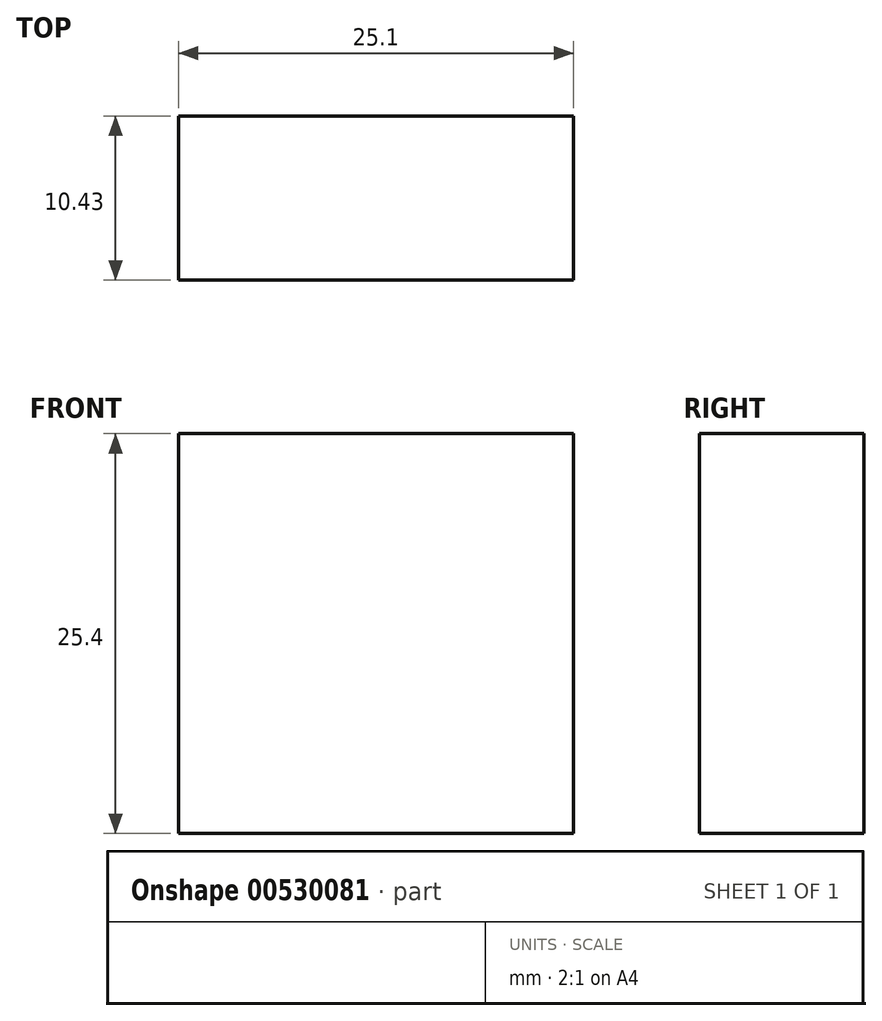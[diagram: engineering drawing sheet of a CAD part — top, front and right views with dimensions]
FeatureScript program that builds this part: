
annotation { "Feature Type Name" : "Feature", "Feature Type Description" : "" }
export const myFeature = defineFeature(function(context is Context, id is Id, definition is map)
    precondition{}
    {
        {
            var Q0;
            Q0=qCreatedBy(makeId("Top.planeOp"),FACE);
            var sketch = newSketch(context, id + "F0", { "sketchPlane" : qUnion([Q0])});
            skLineSegment(sketch, "E0", {"start": v(45.07, -18.4) * mm, "end": v(-42.5, -6.13) * mm});
            skLineSegment(sketch, "E1", {"start": v(-38.27, -6.73) * mm, "end": v(-38.27, 20.97) * mm});
            skLineSegment(sketch, "E2", {"start": v(-38.27, 20.97) * mm, "end": v(-23.96, 29.8) * mm});
            skLineSegment(sketch, "E3", {"start": v(-38.27, 20.97) * mm, "end": v(-57.62, 29.8) * mm});
            skLineSegment(sketch, "E4", {"start": v(16.5, -14.4) * mm, "end": v(19.96, 10.25) * mm});
            skLineSegment(sketch, "E5.bottom", {"start": v(7.13, 20.68) * mm, "end": v(32.23, 20.68) * mm});
            skLineSegment(sketch, "E5.top", {"start": v(7.13, 10.25) * mm, "end": v(32.23, 10.25) * mm});
            skLineSegment(sketch, "E5.left", {"start": v(7.13, 20.68) * mm, "end": v(7.13, 10.25) * mm});
            skLineSegment(sketch, "E5.right", {"start": v(32.23, 20.68) * mm, "end": v(32.23, 10.25) * mm});
            skLineSegment(sketch, "E6", {"start": v(-41.07, -39.5) * mm, "end": v(-41.07, -72.88) * mm});
            skLineSegment(sketch, "E7", {"start": v(-41.07, -39.5) * mm, "end": v(-15.4, -61.18) * mm});
            skLineSegment(sketch, "E8", {"start": v(-41.07, -39.5) * mm, "end": v(-7.42, -33.8) * mm});
            skLineSegment(sketch, "E9", {"start": v(-41.07, -39.5) * mm, "end": v(-23.96, -12.12) * mm});
            skLineSegment(sketch, "E10", {"start": v(-41.07, -39.5) * mm, "end": v(-53.05, -9.56) * mm});
            skLineSegment(sketch, "E11", {"start": v(-41.07, -39.5) * mm, "end": v(-72.45, -33.8) * mm});
            skLineSegment(sketch, "E12", {"start": v(-41.07, -39.5) * mm, "end": v(-67.03, -61.18) * mm});
            skLineSegment(sketch, "E13", {"start": v(48.78, -42.64) * mm, "end": v(45.07, -18.4) * mm});
            skLineSegment(sketch, "E14", {"start": v(48.78, -42.64) * mm, "end": v(60.97, -23.13) * mm});
            skLineSegment(sketch, "E15", {"start": v(48.78, -42.64) * mm, "end": v(71.46, -39.17) * mm});
            skLineSegment(sketch, "E16", {"start": v(48.78, -42.64) * mm, "end": v(68.06, -54.7) * mm});
            skLineSegment(sketch, "E17", {"start": v(48.78, -42.64) * mm, "end": v(52.45, -66.7) * mm});
            skLineSegment(sketch, "E18", {"start": v(48.78, -42.64) * mm, "end": v(35.48, -63.92) * mm});
            skLineSegment(sketch, "E19", {"start": v(35.66, -64.04) * mm, "end": v(48.78, -42.64) * mm});
            skLineSegment(sketch, "E20", {"start": v(48.78, -42.64) * mm, "end": v(30.52, -26.96) * mm});
            skLineSegment(sketch, "E21", {"start": v(48.78, -42.64) * mm, "end": v(24, -46.43) * mm});
            skSolve(sketch);
        }
        {
            var Q0;
            Q0=makeQuery(id+"F0.imprint","IMPRINT",FACE,{"disambiguationData":[TD([[makeQuery(id+"F0.imprint","IMPRINT",EDGE,{"derivedFrom":sQuery(id+"F0.wireOp",EDGE,"E5.bottom")}),-1.0]])]});
            extrude(context, id + "F1", {"entities" : qUnion([Q0]), "depth" : 25.4 * mm, "offsetDistance" : 25.4 * mm});
        }
    });
